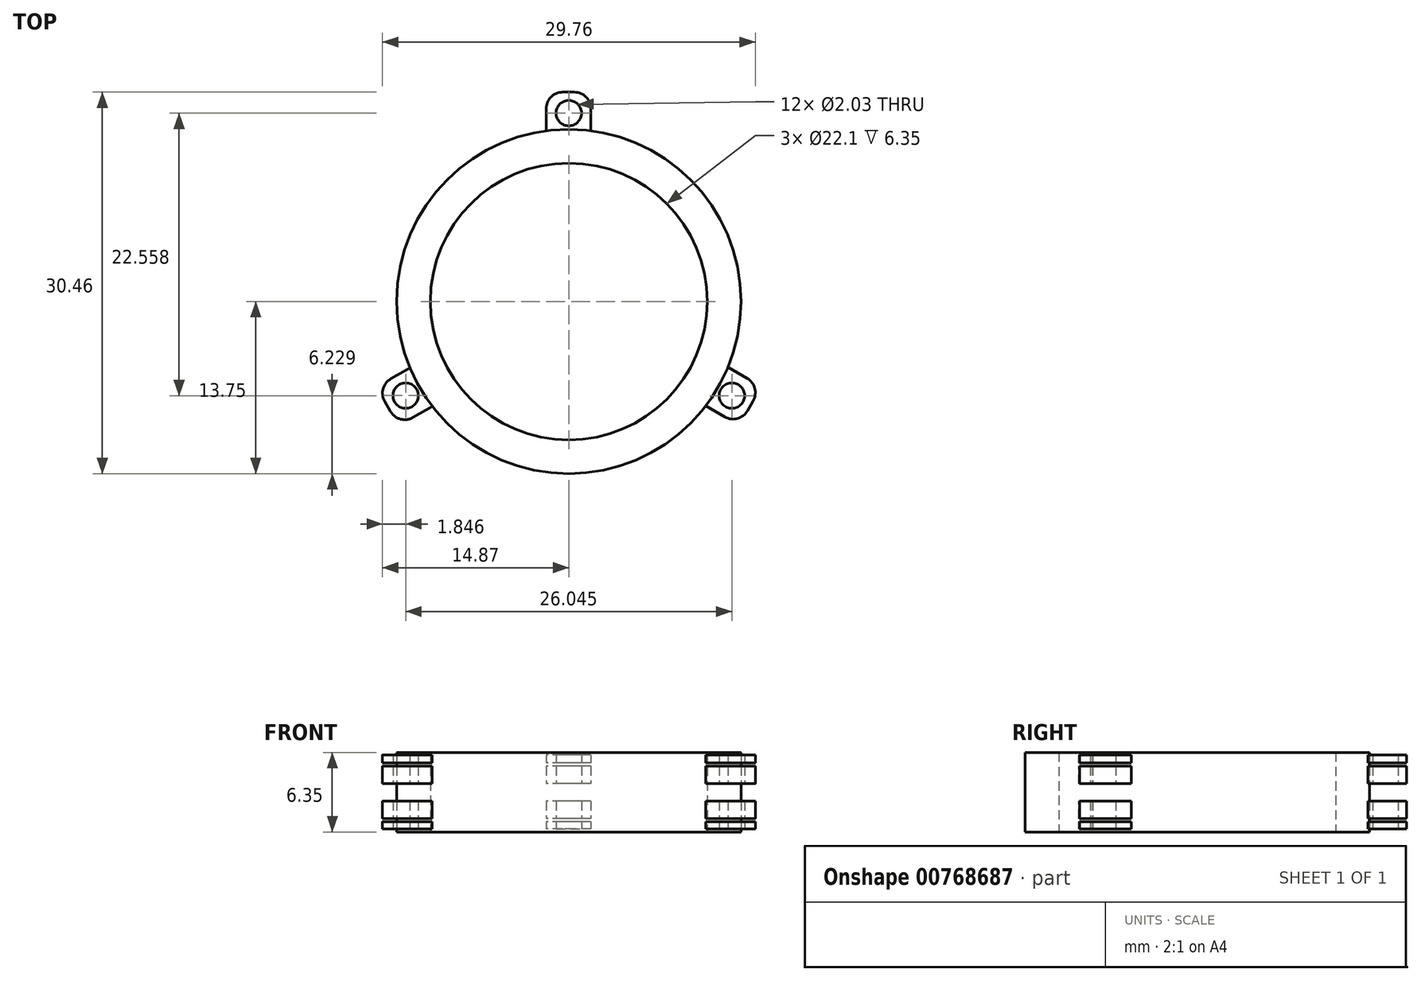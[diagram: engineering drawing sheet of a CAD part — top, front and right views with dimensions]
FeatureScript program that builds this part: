
annotation { "Feature Type Name" : "Feature", "Feature Type Description" : "" }
export const myFeature = defineFeature(function(context is Context, id is Id, definition is map)
    precondition{}
    {
        {
            var Q0;
            Q0=qCreatedBy(makeId("Top.planeOp"),FACE);
            var sketch = newSketch(context, id + "F0", { "sketchPlane" : qUnion([Q0])});
            skCircle(sketch, "E0", {"center": v(0, 0) * mm, "radius": 13.75 * mm});
            skCircle(sketch, "E1", {"center": v(0, 0) * mm, "radius": 11.05 * mm});
            skLineSegment(sketch, "E2", {"start": v(0, 0) * mm, "end": v(0, 26.56) * mm, "construction": true});
            skLineSegment(sketch, "E3.1.0", {"start": v(0, 0) * mm, "end": v(-23, -13.28) * mm, "construction": true});
            skLineSegment(sketch, "E3.2.0", {"start": v(0, 0) * mm, "end": v(23, -13.28) * mm, "construction": true});
            skSolve(sketch);
        }
        {
            var Q0;
            Q0 = qSketchRegion(id + "F0", true);
            extrude(context, id + "F1", {"entities" : qUnion([Q0]), "depth" : 6.35 * mm, "offsetDistance" : 25.4 * mm});
        }
        {
            var Q0;
            Q0=qCreatedBy(makeId("Front.planeOp"),FACE);
            var sketch = newSketch(context, id + "F2", { "sketchPlane" : qUnion([Q0])});
            skLineSegment(sketch, "E4", {"start": v(0.02, 0.83) * mm, "end": v(0, 5.25) * mm, "construction": true});
            skPoint(sketch, "E5", {"position": v(0.01, 2.85) * mm});
            skLineSegment(sketch, "E6.bottom", {"start": v(2.8, 1.07) * mm, "end": v(-2.8, 1.07) * mm});
            skLineSegment(sketch, "E6.top", {"start": v(2.8, 5.25) * mm, "end": v(-2.8, 5.25) * mm});
            skLineSegment(sketch, "E6.left", {"start": v(2.8, 1.07) * mm, "end": v(2.8, 5.25) * mm});
            skLineSegment(sketch, "E6.right", {"start": v(-2.8, 1.07) * mm, "end": v(-2.8, 5.25) * mm});
            skLineSegment(sketch, "E7.bottom", {"start": v(2.8, 2.46) * mm, "end": v(-2.8, 2.46) * mm});
            skLineSegment(sketch, "E7.top", {"start": v(2.8, 3.86) * mm, "end": v(-2.8, 3.86) * mm});
            skLineSegment(sketch, "E7.left", {"start": v(2.8, 2.13) * mm, "end": v(2.8, 3.52) * mm});
            skLineSegment(sketch, "E7.right", {"start": v(-2.8, 2.13) * mm, "end": v(-2.8, 3.52) * mm});
            skLineSegment(sketch, "E8", {"start": v(1.76, 1.07) * mm, "end": v(1.76, 5.25) * mm});
            skLineSegment(sketch, "E9", {"start": v(-1.8, 1.07) * mm, "end": v(-1.8, 5.25) * mm});
            skPoint(sketch, "E10.orphan", {"position": v(0, 4.86) * mm});
            skLineSegment(sketch, "E11.bottom", {"start": v(1.76, 1.07) * mm, "end": v(-2.8, 1.07) * mm});
            skLineSegment(sketch, "E12.bottom", {"start": v(1.76, 5.25) * mm, "end": v(-2.8, 5.25) * mm});
            skPoint(sketch, "E13.endSnap0", {"position": v(-2.8, 0.6) * mm});
            skPoint(sketch, "E14.orphan", {"position": v(-2.8, 6.13) * mm});
            skPoint(sketch, "E15.orphan", {"position": v(-2.8, 0.83) * mm});
            skPoint(sketch, "E16.orphan", {"position": v(-2.8, 0.14) * mm});
            skLineSegment(sketch, "E17.bottom", {"start": v(1.76, 1.07) * mm, "end": v(-1.8, 1.07) * mm});
            skLineSegment(sketch, "E17.top", {"start": v(1.76, 0.25) * mm, "end": v(-1.8, 0.25) * mm});
            skLineSegment(sketch, "E17.left", {"start": v(1.76, 1.07) * mm, "end": v(1.76, 0.25) * mm});
            skLineSegment(sketch, "E17.right", {"start": v(-1.8, 1.07) * mm, "end": v(-1.8, 0.25) * mm});
            skLineSegment(sketch, "E18.top", {"start": v(1.76, 0.82) * mm, "end": v(-1.8, 0.82) * mm});
            skLineSegment(sketch, "E18.left", {"start": v(1.76, 1.07) * mm, "end": v(1.76, 0.82) * mm});
            skLineSegment(sketch, "E18.right", {"start": v(-1.8, 1.07) * mm, "end": v(-1.8, 0.82) * mm});
            skLineSegment(sketch, "E19.bottom", {"start": v(1.76, 5.25) * mm, "end": v(-1.8, 5.25) * mm});
            skLineSegment(sketch, "E19.top", {"start": v(1.76, 6.15) * mm, "end": v(-1.8, 6.15) * mm});
            skLineSegment(sketch, "E19.left", {"start": v(1.76, 5.25) * mm, "end": v(1.76, 6.15) * mm});
            skLineSegment(sketch, "E19.right", {"start": v(-1.8, 5.25) * mm, "end": v(-1.8, 6.15) * mm});
            skLineSegment(sketch, "E20.top", {"start": v(1.76, 5.52) * mm, "end": v(-1.8, 5.52) * mm});
            skLineSegment(sketch, "E20.left", {"start": v(1.76, 5.25) * mm, "end": v(1.76, 5.52) * mm});
            skLineSegment(sketch, "E20.right", {"start": v(-1.8, 5.25) * mm, "end": v(-1.8, 5.52) * mm});
            skSolve(sketch);
        }
        {
            var Q0;
            {var subQ0=sQuery(id+"F2.wireOp",EDGE,"E8");var subQ1=sQuery(id+"F2.wireOp",EDGE,"E7.top");var subQ2=makeQuery(id+"F2.imprint","INTERSECT",VERTEX,{"derivedFrom":[subQ1,subQ0]});Q0=makeQuery(id+"F2.imprint","IMPRINT",FACE,{"disambiguationData":[TD([[makeQuery(id+"F2.imprint","IMPRINT",EDGE,{"disambiguationData":[TD([[subQ2,-1.0]])],"derivedFrom":subQ1}),-1.0]])]});}
            var Q1;
            {var subQ0=sQuery(id+"F2.wireOp",EDGE,"E8");var subQ1=sQuery(id+"F2.wireOp",EDGE,"E7.bottom");var subQ2=makeQuery(id+"F2.imprint","INTERSECT",VERTEX,{"derivedFrom":[subQ1,subQ0]});Q1=makeQuery(id+"F2.imprint","IMPRINT",FACE,{"disambiguationData":[TD([[makeQuery(id+"F2.imprint","IMPRINT",EDGE,{"disambiguationData":[TD([[subQ2,-1.0]])],"derivedFrom":subQ1}),1.0]])]});}
            var Q2;
            Q2=makeQuery(id+"F2.imprint","IMPRINT",FACE,{"disambiguationData":[TD([[makeQuery(id+"F2.imprint","IMPRINT",EDGE,{"derivedFrom":sQuery(id+"F2.wireOp",EDGE,"E17.top")}),-1.0]])]});
            var Q3;
            Q3=makeQuery(id+"F2.imprint","IMPRINT",FACE,{"disambiguationData":[TD([[makeQuery(id+"F2.imprint","IMPRINT",EDGE,{"derivedFrom":sQuery(id+"F2.wireOp",EDGE,"E19.top")}),1.0]])]});
            extrude(context, id + "F3", {"entities" : qUnion([Q0, Q1, Q2, Q3]), "operationType" : NewBodyOperationType.ADD, "oppositeDirection" : true, "depth" : 16.71 * mm, "offsetDistance" : 25.4 * mm, "hasSecondDirection" : true, "secondDirectionOppositeDirection" : true, "secondDirectionDepth" : 13.46 * mm});
        }
        {
            var Q0;
            Q0=makeQuery(id+"F3.opExtrude","SWEPT_FACE",FACE,{"disambiguationData":[OSD([sQuery(id+"F2.wireOp",EDGE,"E17.top")])]});
            var sketch = newSketch(context, id + "F4", { "sketchPlane" : qUnion([Q0])});
            skLineSegment(sketch, "E21", {"start": v(0, -13.64) * mm, "end": v(0, -16.43) * mm, "construction": true});
            skPoint(sketch, "E21.endSnap0", {"position": v(0, 13.59) * mm});
            skCircle(sketch, "E22", {"center": v(0, -15.04) * mm, "radius": 1.02 * mm});
            skSolve(sketch);
        }
        {
            var Q0;
            Q0=makeQuery(id+"F4.imprint","IMPRINT",FACE,{"disambiguationData":[TD([[makeQuery(id+"F4.imprint","IMPRINT",EDGE,{"derivedFrom":sQuery(id+"F4.wireOp",EDGE,"E22")}),1.0]])]});
            var Q1;
            Q1=sQuery(id+"F4.wireOp",EDGE,"E22");
            extrude(context, id + "F5", {"entities" : qUnion([Q0]), "operationType" : NewBodyOperationType.REMOVE, "surfaceEntities" : qUnion([Q1]), "oppositeDirection" : true, "depth" : 25.4 * mm, "offsetDistance" : 25.4 * mm});
        }
        {
            var Q0;
            Q0=makeQuery(id+"F3.opExtrude","CAP_EDGE",EDGE,{"disambiguationData":[OSD([sQuery(id+"F2.wireOp",EDGE,"wJNCDDMg-mcV2-Jskm-efVg-1sbTeijP1O9N")])],"isStart":false});
            var Q1;
            Q1=makeQuery(id+"F3.opExtrude","CAP_EDGE",EDGE,{"disambiguationData":[OSD([sQuery(id+"F2.wireOp",EDGE,"BX0AkwTY-Dvhm-Ub2w-31rT-KtFGOmj5SkaS")])],"isStart":false});
            var Q2;
            Q2=makeQuery(id+"F3.opExtrude","CAP_EDGE",EDGE,{"disambiguationData":[OSD([sQuery(id+"F2.wireOp",EDGE,"i0wjqYCB-AnTl-rZ55-qdCH-2eDlRtjBy8CS")])],"isStart":false});
            var Q3;
            Q3=makeQuery(id+"F3.opExtrude","CAP_EDGE",EDGE,{"disambiguationData":[OSD([sQuery(id+"F2.wireOp",EDGE,"0H9Wo8xZ-OHsT-pqPI-XAvV-ywjx5OgmA5lt")])],"isStart":false});
            var Q4;
            {var subQ0=sQuery(id+"F2.wireOp",EDGE,"b481c2c5-0aff-463e-a399-628b8af691e80.MirrorCS");Q4=makeQuery(id+"F3.opExtrude","CAP_EDGE",EDGE,{"disambiguationData":[OSD([subQ0]),TDD([makeQuery(id+"F2.imprint","IMPRINT",EDGE,{"disambiguationData":[TD([[makeQuery(id+"F2.imprint","INTERSECT",VERTEX,{"derivedFrom":[subQ0,sQuery(id+"F2.wireOp",EDGE,"7eYHgRKW-t6kR-3vbi-M1bu-JxcqkB0VW207")]}),1.0]])],"derivedFrom":subQ0})])],"isStart":false});}
            var Q5;
            {var subQ0=sQuery(id+"F2.wireOp",EDGE,"hqYwq7rJ-d2fg-T8mY-De6B-lo0S8pHOss8T");Q5=makeQuery(id+"F3.opExtrude","CAP_EDGE",EDGE,{"disambiguationData":[OSD([subQ0]),TDD([makeQuery(id+"F2.imprint","IMPRINT",EDGE,{"disambiguationData":[TD([[makeQuery(id+"F2.imprint","INTERSECT",VERTEX,{"derivedFrom":[sQuery(id+"F2.wireOp",EDGE,"cb185676-e843-479b-b432-559dd6952236.bottom"),subQ0]}),1.0]])],"derivedFrom":subQ0})])],"isStart":false});}
            var Q6;
            {var subQ0=sQuery(id+"F2.wireOp",EDGE,"hqYwq7rJ-d2fg-T8mY-De6B-lo0S8pHOss8T");Q6=makeQuery(id+"F3.opExtrude","CAP_EDGE",EDGE,{"disambiguationData":[OSD([subQ0]),TDD([makeQuery(id+"F2.imprint","IMPRINT",EDGE,{"disambiguationData":[TD([[makeQuery(id+"F2.imprint","INTERSECT",VERTEX,{"derivedFrom":[sQuery(id+"F2.wireOp",EDGE,"cb185676-e843-479b-b432-559dd6952236.top"),subQ0]}),-1.0]])],"derivedFrom":subQ0})])],"isStart":false});}
            var Q7;
            {var subQ0=sQuery(id+"F2.wireOp",EDGE,"b481c2c5-0aff-463e-a399-628b8af691e80.MirrorCS");Q7=makeQuery(id+"F3.opExtrude","CAP_EDGE",EDGE,{"disambiguationData":[OSD([subQ0]),TDD([makeQuery(id+"F2.imprint","IMPRINT",EDGE,{"disambiguationData":[TD([[makeQuery(id+"F2.imprint","INTERSECT",VERTEX,{"derivedFrom":[sQuery(id+"F2.wireOp",EDGE,"cb185676-e843-479b-b432-559dd6952236.top"),subQ0]}),-1.0]])],"derivedFrom":subQ0})])],"isStart":false});}
            var Q8;
            {var subQ0=sQuery(id+"F2.wireOp",EDGE,"b481c2c5-0aff-463e-a399-628b8af691e80.MirrorCS");var subQ1=makeQuery(id+"F2.imprint","IMPRINT",VERTEX,{"derivedFrom":subQ0});Q8=makeQuery(id+"F3.opExtrude","CAP_EDGE",EDGE,{"disambiguationData":[OSD([subQ0]),TDD([makeQuery(id+"F2.imprint","IMPRINT",EDGE,{"disambiguationData":[TD([[subQ1,1.0]])],"derivedFrom":subQ0}),makeQuery(id+"F2.imprint","IMPRINT",EDGE,{"disambiguationData":[TD([[subQ1,-1.0]])],"derivedFrom":subQ0})])],"isStart":false});}
            var Q9;
            {var subQ0=sQuery(id+"F2.wireOp",EDGE,"E8");Q9=makeQuery(id+"F3.opExtrude","CAP_EDGE",EDGE,{"disambiguationData":[OSD([subQ0]),TDD([makeQuery(id+"F2.imprint","IMPRINT",EDGE,{"disambiguationData":[TD([[makeQuery(id+"F2.imprint","INTERSECT",VERTEX,{"derivedFrom":[sQuery(id+"F2.wireOp",EDGE,"E6.bottom"),subQ0]}),-1.0]])],"derivedFrom":subQ0})])],"isStart":false});}
            var Q10;
            {var subQ0=sQuery(id+"F2.wireOp",EDGE,"E8");Q10=makeQuery(id+"F3.opExtrude","CAP_EDGE",EDGE,{"disambiguationData":[OSD([subQ0]),TDD([makeQuery(id+"F2.imprint","IMPRINT",EDGE,{"disambiguationData":[TD([[makeQuery(id+"F2.imprint","INTERSECT",VERTEX,{"derivedFrom":[sQuery(id+"F2.wireOp",EDGE,"E6.top"),subQ0]}),1.0]])],"derivedFrom":subQ0})])],"isStart":false});}
            var Q11;
            {var subQ0=sQuery(id+"F2.wireOp",EDGE,"E9");Q11=makeQuery(id+"F3.opExtrude","CAP_EDGE",EDGE,{"disambiguationData":[OSD([subQ0]),TDD([makeQuery(id+"F2.imprint","IMPRINT",EDGE,{"disambiguationData":[TD([[makeQuery(id+"F2.imprint","INTERSECT",VERTEX,{"derivedFrom":[sQuery(id+"F2.wireOp",EDGE,"E6.top"),subQ0]}),1.0]])],"derivedFrom":subQ0})])],"isStart":false});}
            var Q12;
            {var subQ0=sQuery(id+"F2.wireOp",EDGE,"E9");Q12=makeQuery(id+"F3.opExtrude","CAP_EDGE",EDGE,{"disambiguationData":[OSD([subQ0]),TDD([makeQuery(id+"F2.imprint","IMPRINT",EDGE,{"disambiguationData":[TD([[makeQuery(id+"F2.imprint","INTERSECT",VERTEX,{"derivedFrom":[sQuery(id+"F2.wireOp",EDGE,"E6.bottom"),subQ0]}),-1.0]])],"derivedFrom":subQ0})])],"isStart":false});}
            var Q13;
            Q13=makeQuery(id+"F3.opExtrude","CAP_EDGE",EDGE,{"disambiguationData":[OSD([sQuery(id+"F2.wireOp",EDGE,"E17.left")])],"isStart":false});
            var Q14;
            Q14=makeQuery(id+"F3.opExtrude","CAP_EDGE",EDGE,{"disambiguationData":[OSD([sQuery(id+"F2.wireOp",EDGE,"E17.right")])],"isStart":false});
            var Q15;
            Q15=makeQuery(id+"F3.opExtrude","CAP_EDGE",EDGE,{"disambiguationData":[OSD([sQuery(id+"F2.wireOp",EDGE,"E19.right")])],"isStart":false});
            var Q16;
            Q16=makeQuery(id+"F3.opExtrude","CAP_EDGE",EDGE,{"disambiguationData":[OSD([sQuery(id+"F2.wireOp",EDGE,"E19.left")])],"isStart":false});
            fillet(context, id + "F6", {"entities" : qUnion([Q0, Q1, Q2, Q3, Q4, Q5, Q6, Q7, Q8, Q9, Q10, Q11, Q12, Q13, Q14, Q15, Q16]), "radius" : 1.32 * mm, "tangentPropagation" : true, "allowEdgeOverflow" : false});
        }
        {
            var Q0;
            Q0=makeQuery(id+"F1.opExtrude","SWEPT_BODY",BODY,{"disambiguationData":[OSD([sQuery(id+"F0.wireOp",EDGE,"E0"),sQuery(id+"F0.wireOp",EDGE,"E1")])]});
            var Q1;
            Q1=makeQuery(id+"F1.opExtrude","CAP_EDGE",EDGE,{"disambiguationData":[OSD([sQuery(id+"F0.wireOp",EDGE,"E1")])],"isStart":false});
            circularPattern(context, id + "F7", {"entities" : qUnion([Q0]), "axis" : qUnion([Q1]), "angle" : 360 * degree, "instanceCount" : 3, "equalSpace" : true, "computeTransformsWithoutBuiltin" : true});
        }
    });
